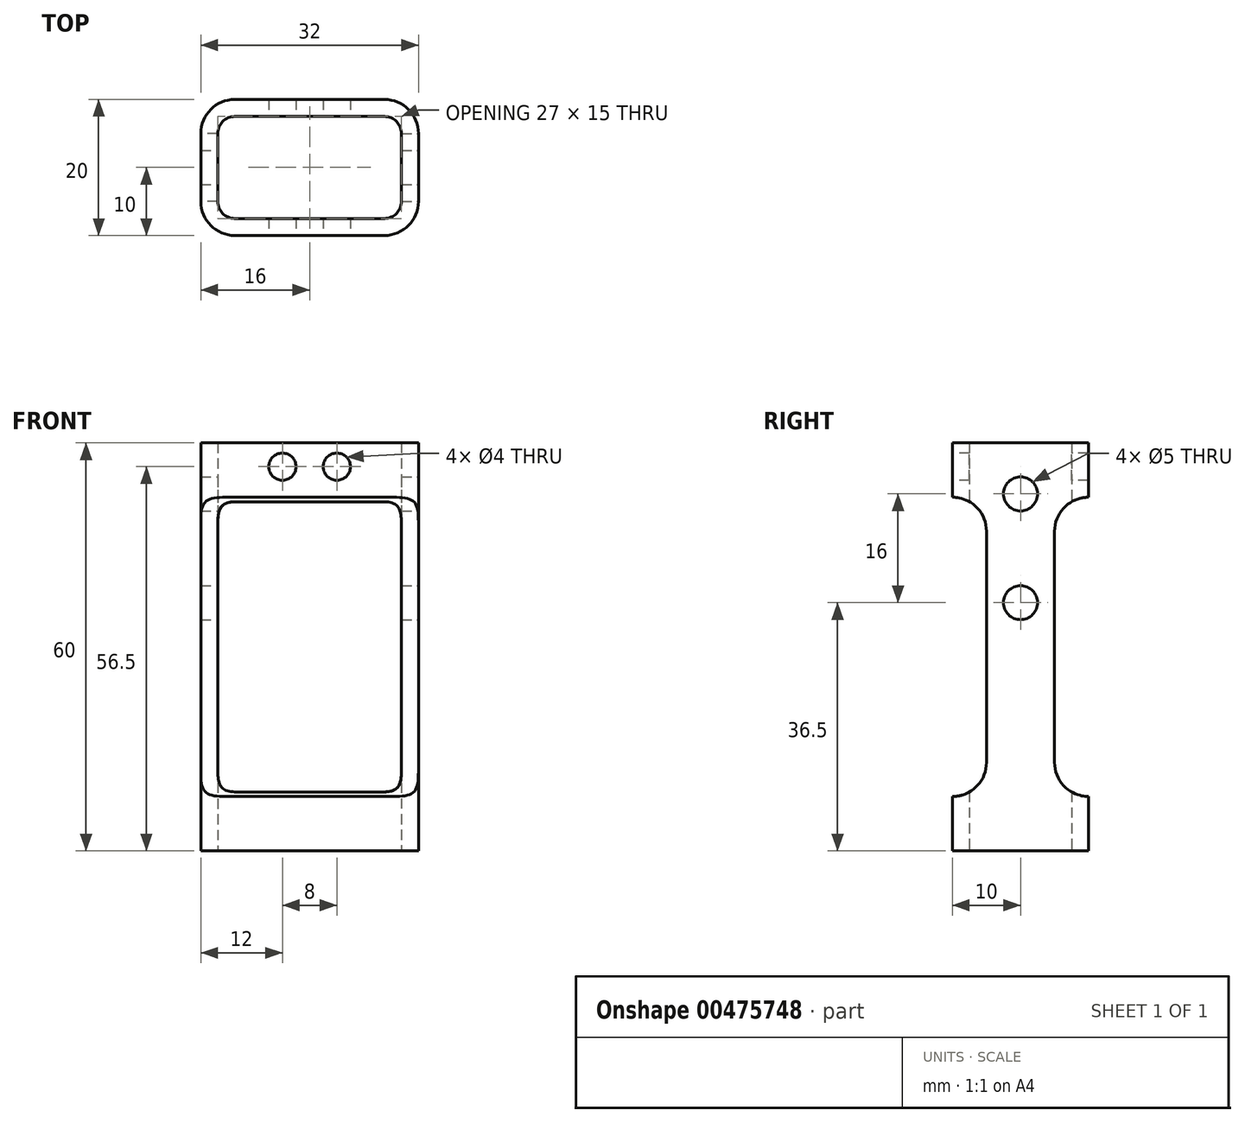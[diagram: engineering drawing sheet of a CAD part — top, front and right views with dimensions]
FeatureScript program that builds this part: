
annotation { "Feature Type Name" : "Feature", "Feature Type Description" : "" }
export const myFeature = defineFeature(function(context is Context, id is Id, definition is map)
    precondition{}
    {
        {
            var Q0;
            Q0=qCreatedBy(makeId("Top.planeOp"),FACE);
            var sketch = newSketch(context, id + "F0", { "sketchPlane" : qUnion([Q0])});
            skLineSegment(sketch, "E0.bottom", {"start": v(11, -7.5) * mm, "end": v(-11, -7.5) * mm});
            skLineSegment(sketch, "E0.top", {"start": v(11, 7.5) * mm, "end": v(-11, 7.5) * mm});
            skLineSegment(sketch, "E0.left", {"start": v(13.5, -5) * mm, "end": v(13.5, 5) * mm});
            skLineSegment(sketch, "E0.right", {"start": v(-13.5, -5) * mm, "end": v(-13.5, 5) * mm});
            skPoint(sketch, "E0.middle", {"position": v(0, 0) * mm});
            skPoint(sketch, "E1.visualSharp", {"position": v(-13.5, 7.5) * mm});
            skArc(sketch, "E1.filletArc", {"start": v(-11, 7.5) * mm, "mid": v(-12.77, 6.77) * mm, "end": v(-13.5, 5) * mm});
            skPoint(sketch, "E2.visualSharp", {"position": v(-13.5, -7.5) * mm});
            skArc(sketch, "E2.filletArc", {"start": v(-13.5, -5) * mm, "mid": v(-12.77, -6.77) * mm, "end": v(-11, -7.5) * mm});
            skPoint(sketch, "E3.visualSharp", {"position": v(13.5, -7.5) * mm});
            skArc(sketch, "E3.filletArc", {"start": v(11, -7.5) * mm, "mid": v(12.77, -6.77) * mm, "end": v(13.5, -5) * mm});
            skPoint(sketch, "E4.visualSharp", {"position": v(13.5, 7.5) * mm});
            skArc(sketch, "E4.filletArc", {"start": v(13.5, 5) * mm, "mid": v(12.77, 6.77) * mm, "end": v(11, 7.5) * mm});
            skArc(sketch, "E5.0", {"start": v(16, 5) * mm, "mid": v(14.54, 8.54) * mm, "end": v(11, 10) * mm});
            skLineSegment(sketch, "E5.1", {"start": v(16, -5) * mm, "end": v(16, 5) * mm});
            skLineSegment(sketch, "E5.2", {"start": v(11, 10) * mm, "end": v(-11, 10) * mm});
            skArc(sketch, "E5.3", {"start": v(11, -10) * mm, "mid": v(14.54, -8.54) * mm, "end": v(16, -5) * mm});
            skArc(sketch, "E5.4", {"start": v(-11, 10) * mm, "mid": v(-14.54, 8.54) * mm, "end": v(-16, 5) * mm});
            skLineSegment(sketch, "E5.5", {"start": v(-16, -5) * mm, "end": v(-16, 5) * mm});
            skArc(sketch, "E5.6", {"start": v(-16, -5) * mm, "mid": v(-14.54, -8.54) * mm, "end": v(-11, -10) * mm});
            skLineSegment(sketch, "E5.7", {"start": v(11, -10) * mm, "end": v(-11, -10) * mm});
            skSolve(sketch);
        }
        {
            var Q0;
            Q0=makeQuery(id+"F0.imprint","IMPRINT",FACE,{"disambiguationData":[TD([[makeQuery(id+"F0.imprint","IMPRINT",EDGE,{"derivedFrom":sQuery(id+"F0.wireOp",EDGE,"E0.bottom")}),1.0]])]});
            extrude(context, id + "F1", {"entities" : qUnion([Q0]), "depth" : 60 * mm});
        }
        {
            var Q0;
            Q0=qCreatedBy(makeId("Right.planeOp"),FACE);
            cPlane(context, id + "F2", {"entities" : qUnion([Q0]), "cplaneType" : CPlaneType.OFFSET, "offset" : 16 * mm, "width" : 150 * mm, "height" : 150 * mm});
        }
        {
            var Q0;
            Q0=qCreatedBy(id+"F2.planeOp",FACE);
            var sketch = newSketch(context, id + "F3", { "sketchPlane" : qUnion([Q0])});
            skLineSegment(sketch, "E6.bottom", {"start": v(-10, 52) * mm, "end": v(-5, 52) * mm});
            skLineSegment(sketch, "E6.top", {"start": v(-10, 8) * mm, "end": v(-5, 8) * mm});
            skLineSegment(sketch, "E6.left", {"start": v(-10, 52) * mm, "end": v(-10, 8) * mm});
            skLineSegment(sketch, "E6.right", {"start": v(-5, 52) * mm, "end": v(-5, 8) * mm});
            skPoint(sketch, "E7", {"position": v(-10, 30) * mm});
            skLineSegment(sketch, "E8.MirrorCS", {"start": v(10, 52) * mm, "end": v(5, 52) * mm});
            skPoint(sketch, "E9.MirrorP", {"position": v(10, 30) * mm});
            skLineSegment(sketch, "E10.MirrorCS", {"start": v(5, 52) * mm, "end": v(5, 8) * mm});
            skLineSegment(sketch, "E11.MirrorCS", {"start": v(10, 52) * mm, "end": v(10, 8) * mm});
            skLineSegment(sketch, "E12.MirrorCS", {"start": v(10, 8) * mm, "end": v(5, 8) * mm});
            skCircle(sketch, "E13", {"center": v(0, 52.5) * mm, "radius": 2.5 * mm});
            skCircle(sketch, "E14", {"center": v(0, 36.5) * mm, "radius": 2.5 * mm});
            skSolve(sketch);
        }
        {
            var Q0;
            Q0=makeQuery(id+"F3.imprint","IMPRINT",FACE,{"disambiguationData":[TD([[makeQuery(id+"F3.imprint","IMPRINT",EDGE,{"derivedFrom":sQuery(id+"F3.wireOp",EDGE,"E6.bottom")}),-1.0]])]});
            var Q1;
            Q1=makeQuery(id+"F3.imprint","IMPRINT",FACE,{"disambiguationData":[TD([[makeQuery(id+"F3.imprint","IMPRINT",EDGE,{"derivedFrom":sQuery(id+"F3.wireOp",EDGE,"E8.MirrorCS")}),1.0]])]});
            var Q2;
            Q2=makeQuery(id+"F3.imprint","IMPRINT",FACE,{"disambiguationData":[TD([[makeQuery(id+"F3.imprint","IMPRINT",EDGE,{"derivedFrom":sQuery(id+"F3.wireOp",EDGE,"E13")}),1.0]])]});
            var Q3;
            Q3=makeQuery(id+"F3.imprint","IMPRINT",FACE,{"disambiguationData":[TD([[makeQuery(id+"F3.imprint","IMPRINT",EDGE,{"derivedFrom":sQuery(id+"F3.wireOp",EDGE,"E14")}),1.0]])]});
            extrude(context, id + "F4", {"entities" : qUnion([Q0, Q1, Q2, Q3]), "operationType" : NewBodyOperationType.REMOVE, "endBound" : BoundingType.THROUGH_ALL, "oppositeDirection" : true, "depth" : 25 * mm});
        }
        {
            var Q0;
            {var subQ0=sQuery(id+"F3.wireOp",EDGE,"E6.top");var subQ1=sQuery(id+"F3.wireOp",EDGE,"E6.right");Q0=makeQuery(id+"F4.boolean.opBoolean","COPY",EDGE,{"disambiguationData":[TD([makeQuery(id+"F1.opExtrude","SWEPT_FACE",FACE,{"disambiguationData":[OSD([sQuery(id+"F0.wireOp",EDGE,"E0.left")])]})])],"derivedFrom":makeQuery(id+"F4.opExtrude","SWEPT_EDGE",EDGE,{"disambiguationData":[OSD([subQ0,subQ1])]})});}
            var Q1;
            {var subQ0=sQuery(id+"F3.wireOp",EDGE,"E10.MirrorCS");var subQ1=sQuery(id+"F3.wireOp",EDGE,"E12.MirrorCS");Q1=makeQuery(id+"F4.boolean.opBoolean","COPY",EDGE,{"disambiguationData":[TD([makeQuery(id+"F1.opExtrude","SWEPT_FACE",FACE,{"disambiguationData":[OSD([sQuery(id+"F0.wireOp",EDGE,"E0.left")])]})])],"derivedFrom":makeQuery(id+"F4.opExtrude","SWEPT_EDGE",EDGE,{"disambiguationData":[OSD([subQ0,subQ1])]})});}
            var Q2;
            {var subQ0=sQuery(id+"F3.wireOp",EDGE,"E8.MirrorCS");var subQ1=sQuery(id+"F3.wireOp",EDGE,"E10.MirrorCS");Q2=makeQuery(id+"F4.boolean.opBoolean","COPY",EDGE,{"disambiguationData":[TD([makeQuery(id+"F1.opExtrude","SWEPT_FACE",FACE,{"disambiguationData":[OSD([sQuery(id+"F0.wireOp",EDGE,"E0.left")])]})])],"derivedFrom":makeQuery(id+"F4.opExtrude","SWEPT_EDGE",EDGE,{"disambiguationData":[OSD([subQ0,subQ1])]})});}
            var Q3;
            {var subQ0=sQuery(id+"F3.wireOp",EDGE,"E6.bottom");var subQ1=sQuery(id+"F3.wireOp",EDGE,"E6.right");Q3=makeQuery(id+"F4.boolean.opBoolean","COPY",EDGE,{"disambiguationData":[TD([makeQuery(id+"F1.opExtrude","SWEPT_FACE",FACE,{"disambiguationData":[OSD([sQuery(id+"F0.wireOp",EDGE,"E0.left")])]})])],"derivedFrom":makeQuery(id+"F4.opExtrude","SWEPT_EDGE",EDGE,{"disambiguationData":[OSD([subQ0,subQ1])]})});}
            fillet(context, id + "F5", {"entities" : qUnion([Q0, Q1, Q2, Q3]), "radius" : 5 * mm, "tangentPropagation" : true, "allowEdgeOverflow" : false});
        }
        {
            var Q0;
            {var subQ0=sQuery(id+"F0.wireOp",EDGE,"E5.7");Q0=makeQuery(id+"F4.boolean.opBoolean","SPLIT",FACE,{"disambiguationData":[TD([makeQuery(id+"F4.opExtrude","SWEPT_FACE",FACE,{"disambiguationData":[OSD([sQuery(id+"F3.wireOp",EDGE,"E6.bottom")])]})])],"derivedFrom":makeQuery(id+"F1.opExtrude","SWEPT_FACE",FACE,{"disambiguationData":[OSD([subQ0])]})});}
            var sketch = newSketch(context, id + "F6", { "sketchPlane" : qUnion([Q0])});
            skPoint(sketch, "E15", {"position": v(-4, 56.5) * mm});
            skPoint(sketch, "E16.MirrorP", {"position": v(4, 56.5) * mm});
            skSolve(sketch);
        }
        {
            var Q0;
            Q0=sQuery(id+"F6.wireOp",VERTEX,"E15");
            var Q1;
            Q1=sQuery(id+"F6.wireOp",VERTEX,"E16.MirrorP");
            var Q2;
            Q2=makeQuery(id+"F1.opExtrude","SWEPT_BODY",BODY,{"disambiguationData":[OSD([sQuery(id+"F0.wireOp",EDGE,"E0.bottom"),sQuery(id+"F0.wireOp",EDGE,"E0.top"),sQuery(id+"F0.wireOp",EDGE,"E0.left"),sQuery(id+"F0.wireOp",EDGE,"E0.right"),sQuery(id+"F0.wireOp",EDGE,"E1.filletArc"),sQuery(id+"F0.wireOp",EDGE,"E2.filletArc"),sQuery(id+"F0.wireOp",EDGE,"E3.filletArc"),sQuery(id+"F0.wireOp",EDGE,"E4.filletArc"),sQuery(id+"F0.wireOp",EDGE,"E5.0"),sQuery(id+"F0.wireOp",EDGE,"E5.1"),sQuery(id+"F0.wireOp",EDGE,"E5.2"),sQuery(id+"F0.wireOp",EDGE,"E5.3"),sQuery(id+"F0.wireOp",EDGE,"E5.4"),sQuery(id+"F0.wireOp",EDGE,"E5.5"),sQuery(id+"F0.wireOp",EDGE,"E5.6"),sQuery(id+"F0.wireOp",EDGE,"E5.7")])]});
            hole(context, id + "F7", {"style" : HoleStyle.SIMPLE, "endStyle" : HoleEndStyle.THROUGH, "holeDiameter" : 4 * mm, "tappedDepth" : 12 * mm, "tapClearance" : 3, "locations" : qUnion([Q0, Q1]), "scope" : qUnion([Q2])});
        }
    });
